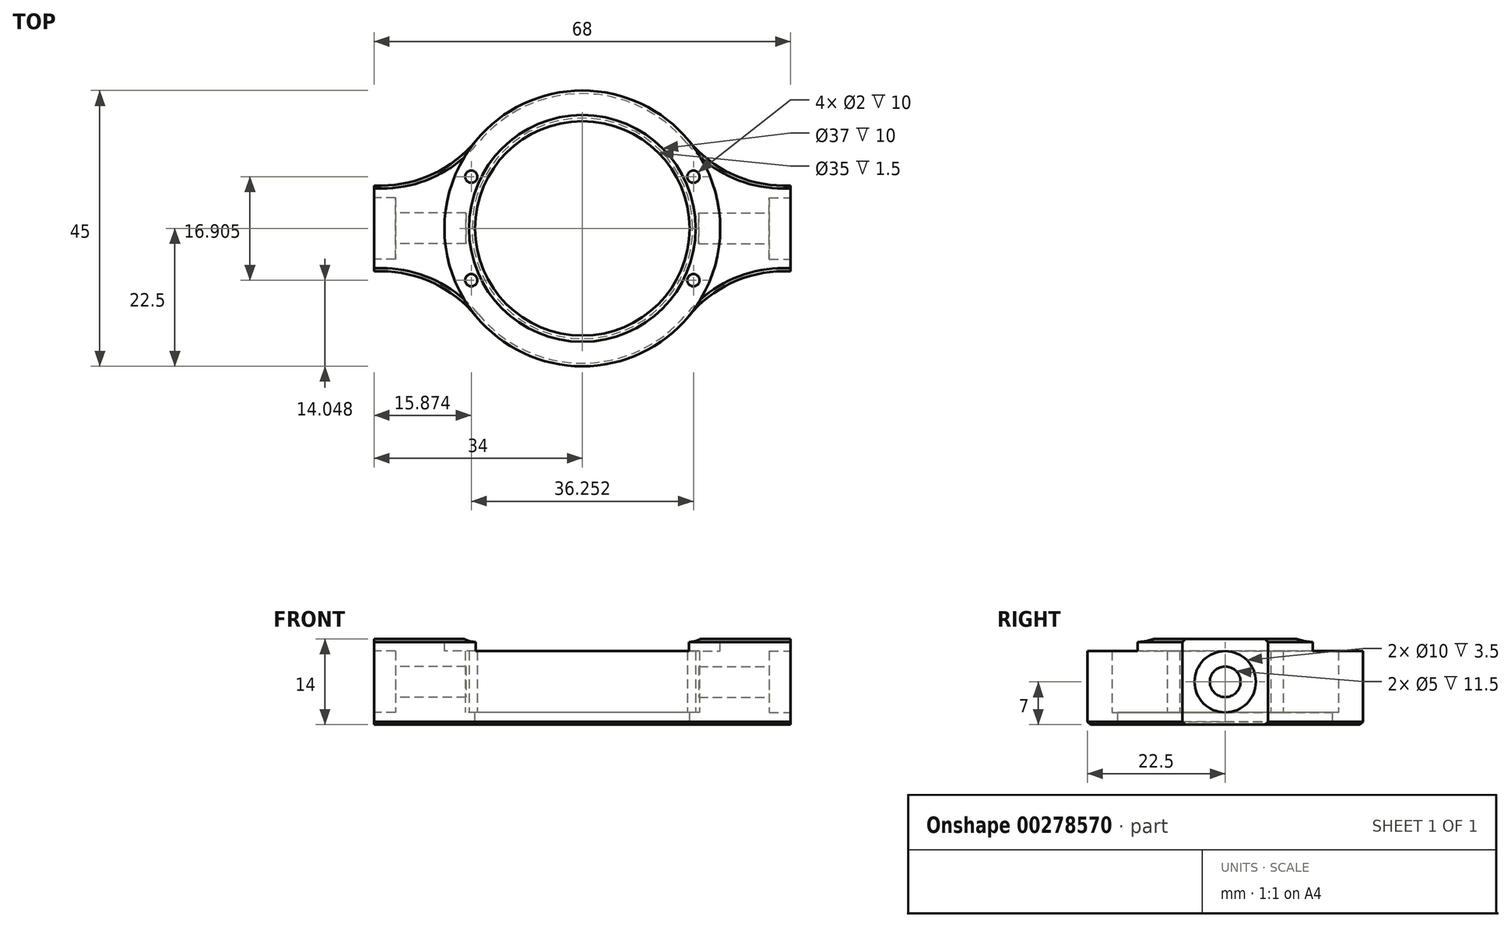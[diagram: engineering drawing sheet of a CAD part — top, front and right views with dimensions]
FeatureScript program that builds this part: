
annotation { "Feature Type Name" : "Feature", "Feature Type Description" : "" }
export const myFeature = defineFeature(function(context is Context, id is Id, definition is map)
    precondition{}
    {
        {
            var Q0;
            Q0=qCreatedBy(makeId("Top.planeOp"),FACE);
            var sketch = newSketch(context, id + "F0", { "sketchPlane" : qUnion([Q0])});
            skCircle(sketch, "E0", {"center": v(0, 0) * mm, "radius": 18.5 * mm});
            skArc(sketch, "E1", {"start": v(21.38, 7) * mm, "mid": v(0, 22.5) * mm, "end": v(-21.38, 7) * mm});
            skLineSegment(sketch, "E2.bottom", {"start": v(34, -7) * mm, "end": v(21.38, -7) * mm});
            skLineSegment(sketch, "E2.top", {"start": v(34, 7) * mm, "end": v(21.38, 7) * mm});
            skLineSegment(sketch, "E2.left", {"start": v(34, -7) * mm, "end": v(34, 7) * mm});
            skLineSegment(sketch, "E2.right", {"start": v(-34, -7) * mm, "end": v(-34, 7) * mm});
            skLineSegment(sketch, "E3.trimOffspring", {"start": v(-21.38, 7) * mm, "end": v(-34, 7) * mm});
            skLineSegment(sketch, "E4.trimOffspring", {"start": v(-21.38, -7) * mm, "end": v(-34, -7) * mm});
            skArc(sketch, "E5.trimOffspring", {"start": v(-21.38, -7) * mm, "mid": v(0, -22.5) * mm, "end": v(21.38, -7) * mm});
            skCircle(sketch, "E6", {"center": v(0, 0) * mm, "radius": 17.5 * mm});
            skLineSegment(sketch, "E7", {"start": v(-80.46, 0) * mm, "end": v(70.78, 0) * mm, "construction": true});
            skLineSegment(sketch, "E8", {"start": v(-80.46, -37.52) * mm, "end": v(70.78, 33) * mm, "construction": true});
            skLineSegment(sketch, "E9", {"start": v(-80.46, 37.52) * mm, "end": v(70.78, -33) * mm, "construction": true});
            skCircle(sketch, "E10", {"center": v(0, 0) * mm, "radius": 20 * mm, "construction": true});
            skCircle(sketch, "E11", {"center": v(18.13, 8.45) * mm, "radius": 1 * mm});
            skCircle(sketch, "E12", {"center": v(18.13, -8.45) * mm, "radius": 1 * mm});
            skCircle(sketch, "E13", {"center": v(-18.13, -8.45) * mm, "radius": 1 * mm});
            skCircle(sketch, "E14", {"center": v(-18.13, 8.45) * mm, "radius": 1 * mm});
            skSolve(sketch);
        }
        {
            var Q0;
            Q0 = qSketchRegion(id + "F0", true);
            extrude(context, id + "F1", {"entities" : qUnion([Q0]), "depth" : 7 * mm, "hasSecondDirection" : true, "secondDirectionOppositeDirection" : true, "secondDirectionDepth" : 7 * mm});
        }
        {
            var Q0;
            Q0=makeQuery(id+"F0.imprint","IMPRINT",FACE,{"disambiguationData":[TD([[makeQuery(id+"F0.imprint","IMPRINT",EDGE,{"derivedFrom":sQuery(id+"F0.wireOp",EDGE,"E0")}),1.0]])]});
            var Q1;
            Q1=makeQuery(id+"F0.imprint","IMPRINT",FACE,{"disambiguationData":[TD([[makeQuery(id+"F0.imprint","IMPRINT",EDGE,{"derivedFrom":sQuery(id+"F0.wireOp",EDGE,"E11")}),1.0]])]});
            var Q2;
            Q2=makeQuery(id+"F0.imprint","IMPRINT",FACE,{"disambiguationData":[TD([[makeQuery(id+"F0.imprint","IMPRINT",EDGE,{"derivedFrom":sQuery(id+"F0.wireOp",EDGE,"E12")}),1.0]])]});
            var Q3;
            Q3=makeQuery(id+"F0.imprint","IMPRINT",FACE,{"disambiguationData":[TD([[makeQuery(id+"F0.imprint","IMPRINT",EDGE,{"derivedFrom":sQuery(id+"F0.wireOp",EDGE,"E13")}),1.0]])]});
            var Q4;
            Q4=makeQuery(id+"F0.imprint","IMPRINT",FACE,{"disambiguationData":[TD([[makeQuery(id+"F0.imprint","IMPRINT",EDGE,{"derivedFrom":sQuery(id+"F0.wireOp",EDGE,"E14")}),1.0]])]});
            extrude(context, id + "F2", {"entities" : qUnion([Q0, Q1, Q2, Q3, Q4]), "operationType" : NewBodyOperationType.ADD, "oppositeDirection" : true, "depth" : 7 * mm, "hasSecondDirection" : true, "secondDirectionOppositeDirection" : false, "secondDirectionDepth" : -5 * mm});
        }
        {
            var Q0;
            Q0=makeQuery(id+"F1.opExtrude","SWEPT_EDGE",EDGE,{"disambiguationData":[OSD([sQuery(id+"F0.wireOp",EDGE,"E1"),sQuery(id+"F0.wireOp",EDGE,"E2.top")])]});
            var Q1;
            Q1=makeQuery(id+"F1.opExtrude","SWEPT_EDGE",EDGE,{"disambiguationData":[OSD([sQuery(id+"F0.wireOp",EDGE,"E2.bottom"),sQuery(id+"F0.wireOp",EDGE,"E5.trimOffspring")])]});
            var Q2;
            Q2=makeQuery(id+"F1.opExtrude","SWEPT_EDGE",EDGE,{"disambiguationData":[OSD([sQuery(id+"F0.wireOp",EDGE,"E4.trimOffspring"),sQuery(id+"F0.wireOp",EDGE,"E5.trimOffspring")])]});
            var Q3;
            Q3=makeQuery(id+"F1.opExtrude","SWEPT_EDGE",EDGE,{"disambiguationData":[OSD([sQuery(id+"F0.wireOp",EDGE,"E1"),sQuery(id+"F0.wireOp",EDGE,"E3.trimOffspring")])]});
            fillet(context, id + "F3", {"entities" : qUnion([Q0, Q1, Q2, Q3]), "radius" : 20 * mm, "tangentPropagation" : true, "allowEdgeOverflow" : false});
        }
        {
            var Q0;
            Q0=makeQuery(id+"F1.opExtrude","CAP_FACE",FACE,{"disambiguationData":[OSD([sQuery(id+"F0.wireOp",EDGE,"E0"),sQuery(id+"F0.wireOp",EDGE,"E1"),sQuery(id+"F0.wireOp",EDGE,"E2.bottom"),sQuery(id+"F0.wireOp",EDGE,"E2.top"),sQuery(id+"F0.wireOp",EDGE,"E2.left"),sQuery(id+"F0.wireOp",EDGE,"E2.right"),sQuery(id+"F0.wireOp",EDGE,"E3.trimOffspring"),sQuery(id+"F0.wireOp",EDGE,"E4.trimOffspring"),sQuery(id+"F0.wireOp",EDGE,"E5.trimOffspring")])],"isStart":false});
            var sketch = newSketch(context, id + "F4", { "sketchPlane" : qUnion([Q0])});
            skCircle(sketch, "E15", {"center": v(0, 0) * mm, "radius": 22.5 * mm});
            skCircle(sketch, "E16", {"center": v(0, 0) * mm, "radius": 17.5 * mm});
            skLineSegment(sketch, "E17", {"start": v(43.77, 0) * mm, "end": v(-49.2, 0) * mm, "construction": true});
            skPoint(sketch, "E17.startSnap0", {"position": v(-34, 0) * mm});
            skPoint(sketch, "E17.endSnap0", {"position": v(-34, 0) * mm});
            skLineSegment(sketch, "E18", {"start": v(-49.2, -22.95) * mm, "end": v(43.77, 20.41) * mm, "construction": true});
            skLineSegment(sketch, "E19", {"start": v(-49.2, 22.95) * mm, "end": v(43.77, -20.41) * mm, "construction": true});
            skCircle(sketch, "E20", {"center": v(0, 0) * mm, "radius": 20 * mm, "construction": true});
            skCircle(sketch, "E21", {"center": v(18.13, 8.45) * mm, "radius": 1 * mm});
            skCircle(sketch, "E22", {"center": v(18.13, -8.45) * mm, "radius": 1 * mm});
            skCircle(sketch, "E23", {"center": v(-18.13, 8.45) * mm, "radius": 1 * mm});
            skCircle(sketch, "E24", {"center": v(-18.13, -8.45) * mm, "radius": 1 * mm});
            skSolve(sketch);
        }
        {
            var Q0;
            {var subQ7=sQuery(id+"F0.wireOp",EDGE,"E0");Q0=makeQuery(id+"F4.imprint","IMPRINT",FACE,{"disambiguationData":[TD([[makeQuery(id+"F4.imprint","IMPRINT",EDGE,{"derivedFrom":makeQuery(id+"F1.opExtrude","CAP_EDGE",EDGE,{"disambiguationData":[OSD([subQ7])],"isStart":false})}),-1.0]])]});}
            var Q1;
            Q1=makeQuery(id+"F4.imprint","IMPRINT",FACE,{"disambiguationData":[TD([[makeQuery(id+"F4.imprint","IMPRINT",EDGE,{"derivedFrom":sQuery(id+"F4.wireOp",EDGE,"E22")}),1.0]])]});
            var Q2;
            Q2=makeQuery(id+"F4.imprint","IMPRINT",FACE,{"disambiguationData":[TD([[makeQuery(id+"F4.imprint","IMPRINT",EDGE,{"derivedFrom":sQuery(id+"F4.wireOp",EDGE,"E21")}),1.0]])]});
            var Q3;
            Q3=makeQuery(id+"F4.imprint","IMPRINT",FACE,{"disambiguationData":[TD([[makeQuery(id+"F4.imprint","IMPRINT",EDGE,{"derivedFrom":sQuery(id+"F4.wireOp",EDGE,"E23")}),1.0]])]});
            var Q4;
            Q4=makeQuery(id+"F4.imprint","IMPRINT",FACE,{"disambiguationData":[TD([[makeQuery(id+"F4.imprint","IMPRINT",EDGE,{"derivedFrom":sQuery(id+"F4.wireOp",EDGE,"E24")}),1.0]])]});
            extrude(context, id + "F5", {"entities" : qUnion([Q0, Q1, Q2, Q3, Q4]), "operationType" : NewBodyOperationType.REMOVE, "oppositeDirection" : true, "depth" : 2 * mm});
        }
        {
            var Q0;
            {var subQ7=sQuery(id+"F0.wireOp",EDGE,"E0");Q0=makeQuery(id+"F4.imprint","IMPRINT",FACE,{"disambiguationData":[TD([[makeQuery(id+"F4.imprint","IMPRINT",EDGE,{"derivedFrom":makeQuery(id+"F1.opExtrude","CAP_EDGE",EDGE,{"disambiguationData":[OSD([subQ7])],"isStart":false})}),-1.0]])]});}
            var Q1;
            Q1=makeQuery(id+"F4.imprint","IMPRINT",FACE,{"disambiguationData":[TD([[makeQuery(id+"F4.imprint","IMPRINT",EDGE,{"derivedFrom":sQuery(id+"F4.wireOp",EDGE,"E16")}),-1.0]])]});
            extrude(context, id + "F6", {"entities" : qUnion([Q0, Q1]), "depth" : -2 * mm});
        }
        {
            var Q0;
            {var subQ0=sQuery(id+"F0.wireOp",EDGE,"E5.trimOffspring");var subQ1=sQuery(id+"F0.wireOp",EDGE,"E4.trimOffspring");Q0=makeQuery(id+"F3.opFillet","BLEND_EDGE",EDGE,{"blendedFrom":[makeQuery(id+"F1.opExtrude","SWEPT_EDGE",EDGE,{"disambiguationData":[OSD([subQ1,subQ0])]}),makeQuery(id+"F1.opExtrude","CAP_FACE",FACE,{"disambiguationData":[OSD([sQuery(id+"F0.wireOp",EDGE,"E0"),sQuery(id+"F0.wireOp",EDGE,"E1"),sQuery(id+"F0.wireOp",EDGE,"E2.bottom"),sQuery(id+"F0.wireOp",EDGE,"E2.top"),sQuery(id+"F0.wireOp",EDGE,"E2.left"),sQuery(id+"F0.wireOp",EDGE,"E2.right"),sQuery(id+"F0.wireOp",EDGE,"E3.trimOffspring"),subQ1,subQ0])],"isStart":false})],"blendedInto":[makeQuery(id+"F1.opExtrude","CAP_FACE",FACE,{"disambiguationData":[OSD([sQuery(id+"F0.wireOp",EDGE,"E0"),sQuery(id+"F0.wireOp",EDGE,"E1"),sQuery(id+"F0.wireOp",EDGE,"E2.bottom"),sQuery(id+"F0.wireOp",EDGE,"E2.top"),sQuery(id+"F0.wireOp",EDGE,"E2.left"),sQuery(id+"F0.wireOp",EDGE,"E2.right"),sQuery(id+"F0.wireOp",EDGE,"E3.trimOffspring"),subQ1,subQ0])],"isStart":false})]});}
            var Q1;
            {var subQ0=sQuery(id+"F0.wireOp",EDGE,"E3.trimOffspring");var subQ1=sQuery(id+"F0.wireOp",EDGE,"E1");Q1=makeQuery(id+"F3.opFillet","BLEND_EDGE",EDGE,{"blendedFrom":[makeQuery(id+"F1.opExtrude","SWEPT_EDGE",EDGE,{"disambiguationData":[OSD([subQ1,subQ0])]}),makeQuery(id+"F1.opExtrude","CAP_FACE",FACE,{"disambiguationData":[OSD([sQuery(id+"F0.wireOp",EDGE,"E0"),subQ1,sQuery(id+"F0.wireOp",EDGE,"E2.bottom"),sQuery(id+"F0.wireOp",EDGE,"E2.top"),sQuery(id+"F0.wireOp",EDGE,"E2.left"),sQuery(id+"F0.wireOp",EDGE,"E2.right"),subQ0,sQuery(id+"F0.wireOp",EDGE,"E4.trimOffspring"),sQuery(id+"F0.wireOp",EDGE,"E5.trimOffspring")])],"isStart":false})],"blendedInto":[makeQuery(id+"F1.opExtrude","CAP_FACE",FACE,{"disambiguationData":[OSD([sQuery(id+"F0.wireOp",EDGE,"E0"),subQ1,sQuery(id+"F0.wireOp",EDGE,"E2.bottom"),sQuery(id+"F0.wireOp",EDGE,"E2.top"),sQuery(id+"F0.wireOp",EDGE,"E2.left"),sQuery(id+"F0.wireOp",EDGE,"E2.right"),subQ0,sQuery(id+"F0.wireOp",EDGE,"E4.trimOffspring"),sQuery(id+"F0.wireOp",EDGE,"E5.trimOffspring")])],"isStart":false})]});}
            var Q2;
            {var subQ0=sQuery(id+"F0.wireOp",EDGE,"E5.trimOffspring");var subQ1=sQuery(id+"F0.wireOp",EDGE,"E2.bottom");Q2=makeQuery(id+"F3.opFillet","BLEND_EDGE",EDGE,{"blendedFrom":[makeQuery(id+"F1.opExtrude","SWEPT_EDGE",EDGE,{"disambiguationData":[OSD([subQ1,subQ0])]}),makeQuery(id+"F1.opExtrude","CAP_FACE",FACE,{"disambiguationData":[OSD([sQuery(id+"F0.wireOp",EDGE,"E0"),sQuery(id+"F0.wireOp",EDGE,"E1"),subQ1,sQuery(id+"F0.wireOp",EDGE,"E2.top"),sQuery(id+"F0.wireOp",EDGE,"E2.left"),sQuery(id+"F0.wireOp",EDGE,"E2.right"),sQuery(id+"F0.wireOp",EDGE,"E3.trimOffspring"),sQuery(id+"F0.wireOp",EDGE,"E4.trimOffspring"),subQ0])],"isStart":false})],"blendedInto":[makeQuery(id+"F1.opExtrude","CAP_FACE",FACE,{"disambiguationData":[OSD([sQuery(id+"F0.wireOp",EDGE,"E0"),sQuery(id+"F0.wireOp",EDGE,"E1"),subQ1,sQuery(id+"F0.wireOp",EDGE,"E2.top"),sQuery(id+"F0.wireOp",EDGE,"E2.left"),sQuery(id+"F0.wireOp",EDGE,"E2.right"),sQuery(id+"F0.wireOp",EDGE,"E3.trimOffspring"),sQuery(id+"F0.wireOp",EDGE,"E4.trimOffspring"),subQ0])],"isStart":false})]});}
            var Q3;
            {var subQ0=sQuery(id+"F0.wireOp",EDGE,"E2.top");var subQ1=sQuery(id+"F0.wireOp",EDGE,"E1");Q3=makeQuery(id+"F3.opFillet","BLEND_EDGE",EDGE,{"blendedFrom":[makeQuery(id+"F1.opExtrude","SWEPT_EDGE",EDGE,{"disambiguationData":[OSD([subQ1,subQ0])]}),makeQuery(id+"F1.opExtrude","CAP_FACE",FACE,{"disambiguationData":[OSD([sQuery(id+"F0.wireOp",EDGE,"E0"),subQ1,sQuery(id+"F0.wireOp",EDGE,"E2.bottom"),subQ0,sQuery(id+"F0.wireOp",EDGE,"E2.left"),sQuery(id+"F0.wireOp",EDGE,"E2.right"),sQuery(id+"F0.wireOp",EDGE,"E3.trimOffspring"),sQuery(id+"F0.wireOp",EDGE,"E4.trimOffspring"),sQuery(id+"F0.wireOp",EDGE,"E5.trimOffspring")])],"isStart":false})],"blendedInto":[makeQuery(id+"F1.opExtrude","CAP_FACE",FACE,{"disambiguationData":[OSD([sQuery(id+"F0.wireOp",EDGE,"E0"),subQ1,sQuery(id+"F0.wireOp",EDGE,"E2.bottom"),subQ0,sQuery(id+"F0.wireOp",EDGE,"E2.left"),sQuery(id+"F0.wireOp",EDGE,"E2.right"),sQuery(id+"F0.wireOp",EDGE,"E3.trimOffspring"),sQuery(id+"F0.wireOp",EDGE,"E4.trimOffspring"),sQuery(id+"F0.wireOp",EDGE,"E5.trimOffspring")])],"isStart":false})]});}
            var Q4;
            {var subQ0=sQuery(id+"F0.wireOp",EDGE,"E0");var subQ1=sQuery(id+"F0.wireOp",EDGE,"E5.trimOffspring");var subQ2=sQuery(id+"F0.wireOp",EDGE,"E2.bottom");Q4=makeQuery(id+"F3.opFillet","BLEND_EDGE",EDGE,{"blendedFrom":[makeQuery(id+"F1.opExtrude","SWEPT_EDGE",EDGE,{"disambiguationData":[OSD([subQ2,subQ1])]}),makeQuery(id+"F2.boolean.opBoolean","MERGE",FACE,{"derivedFrom":[makeQuery(id+"F1.opExtrude","CAP_FACE",FACE,{"disambiguationData":[OSD([subQ0,sQuery(id+"F0.wireOp",EDGE,"E1"),subQ2,sQuery(id+"F0.wireOp",EDGE,"E2.top"),sQuery(id+"F0.wireOp",EDGE,"E2.left"),sQuery(id+"F0.wireOp",EDGE,"E2.right"),sQuery(id+"F0.wireOp",EDGE,"E3.trimOffspring"),sQuery(id+"F0.wireOp",EDGE,"E4.trimOffspring"),subQ1])],"isStart":true}),makeQuery(id+"F2.opExtrude","CAP_FACE",FACE,{"disambiguationData":[OSD([subQ0,sQuery(id+"F0.wireOp",EDGE,"E6")])],"isStart":false})]})],"blendedInto":[makeQuery(id+"F2.boolean.opBoolean","MERGE",FACE,{"derivedFrom":[makeQuery(id+"F1.opExtrude","CAP_FACE",FACE,{"disambiguationData":[OSD([subQ0,sQuery(id+"F0.wireOp",EDGE,"E1"),subQ2,sQuery(id+"F0.wireOp",EDGE,"E2.top"),sQuery(id+"F0.wireOp",EDGE,"E2.left"),sQuery(id+"F0.wireOp",EDGE,"E2.right"),sQuery(id+"F0.wireOp",EDGE,"E3.trimOffspring"),sQuery(id+"F0.wireOp",EDGE,"E4.trimOffspring"),subQ1])],"isStart":true}),makeQuery(id+"F2.opExtrude","CAP_FACE",FACE,{"disambiguationData":[OSD([subQ0,sQuery(id+"F0.wireOp",EDGE,"E6")])],"isStart":false})]})]});}
            var Q5;
            Q5=makeQuery(id+"F1.opExtrude","CAP_EDGE",EDGE,{"disambiguationData":[OSD([sQuery(id+"F0.wireOp",EDGE,"E1")])],"isStart":true});
            var Q6;
            Q6=makeQuery(id+"F2.opExtrude","CAP_EDGE",EDGE,{"disambiguationData":[OSD([sQuery(id+"F0.wireOp",EDGE,"E6")])],"isStart":false});
            var Q7;
            Q7=makeQuery(id+"F5.boolean.opBoolean","COPY",EDGE,{"derivedFrom":makeQuery(id+"F5.opExtrude","CAP_EDGE",EDGE,{"disambiguationData":[OSD([sQuery(id+"F0.wireOp",EDGE,"E0")])],"isStart":false})});
            chamfer(context, id + "F7", {"entities" : qUnion([Q0, Q1, Q2, Q3, Q4, Q5, Q6, Q7]), "width" : 0.5 * mm, "tangentPropagation" : true});
        }
        {
            var Q0;
            Q0=makeQuery(id+"F6.opExtrude","CAP_EDGE",EDGE,{"disambiguationData":[OSD([sQuery(id+"F4.wireOp",EDGE,"E21")])],"isStart":true});
            var Q1;
            Q1=makeQuery(id+"F6.opExtrude","CAP_EDGE",EDGE,{"disambiguationData":[OSD([sQuery(id+"F4.wireOp",EDGE,"E22")])],"isStart":true});
            var Q2;
            Q2=makeQuery(id+"F6.opExtrude","CAP_EDGE",EDGE,{"disambiguationData":[OSD([sQuery(id+"F4.wireOp",EDGE,"E24")])],"isStart":true});
            var Q3;
            Q3=makeQuery(id+"F6.opExtrude","CAP_EDGE",EDGE,{"disambiguationData":[OSD([sQuery(id+"F4.wireOp",EDGE,"E23")])],"isStart":true});
            chamfer(context, id + "F8", {"entities" : qUnion([Q0, Q1, Q2, Q3]), "width" : 1 * mm, "tangentPropagation" : true});
        }
        {
            var Q0;
            Q0=makeQuery(id+"F1.opExtrude","SWEPT_FACE",FACE,{"disambiguationData":[OSD([sQuery(id+"F0.wireOp",EDGE,"E2.right")])]});
            var sketch = newSketch(context, id + "F9", { "sketchPlane" : qUnion([Q0])});
            skCircle(sketch, "E25", {"center": v(0, 0) * mm, "radius": 5 * mm});
            skCircle(sketch, "E26", {"center": v(0, 0) * mm, "radius": 2.5 * mm});
            skSolve(sketch);
        }
        {
            var Q0;
            Q0=makeQuery(id+"F9.imprint","IMPRINT",FACE,{"disambiguationData":[TD([[makeQuery(id+"F9.imprint","IMPRINT",EDGE,{"derivedFrom":sQuery(id+"F9.wireOp",EDGE,"E25")}),1.0]])]});
            var Q1;
            Q1=makeQuery(id+"F9.imprint","IMPRINT",FACE,{"disambiguationData":[TD([[makeQuery(id+"F9.imprint","IMPRINT",EDGE,{"derivedFrom":sQuery(id+"F9.wireOp",EDGE,"E26")}),1.0]])]});
            extrude(context, id + "F10", {"entities" : qUnion([Q0, Q1]), "operationType" : NewBodyOperationType.REMOVE, "oppositeDirection" : true, "depth" : 3.5 * mm});
        }
        {
            var Q0;
            Q0=makeQuery(id+"F9.imprint","IMPRINT",FACE,{"disambiguationData":[TD([[makeQuery(id+"F9.imprint","IMPRINT",EDGE,{"derivedFrom":sQuery(id+"F9.wireOp",EDGE,"E26")}),1.0]])]});
            extrude(context, id + "F11", {"entities" : qUnion([Q0]), "operationType" : NewBodyOperationType.REMOVE, "oppositeDirection" : true, "depth" : 15 * mm});
        }
        {
            var Q0;
            Q0=makeQuery(id+"F1.opExtrude","SWEPT_BODY",BODY,{"disambiguationData":[OSD([sQuery(id+"F0.wireOp",EDGE,"E0"),sQuery(id+"F0.wireOp",EDGE,"E1"),sQuery(id+"F0.wireOp",EDGE,"E2.bottom"),sQuery(id+"F0.wireOp",EDGE,"E2.top"),sQuery(id+"F0.wireOp",EDGE,"E2.left"),sQuery(id+"F0.wireOp",EDGE,"E2.right"),sQuery(id+"F0.wireOp",EDGE,"E3.trimOffspring"),sQuery(id+"F0.wireOp",EDGE,"E4.trimOffspring"),sQuery(id+"F0.wireOp",EDGE,"E5.trimOffspring"),sQuery(id+"F0.wireOp",EDGE,"E11"),sQuery(id+"F0.wireOp",EDGE,"E12"),sQuery(id+"F0.wireOp",EDGE,"E13"),sQuery(id+"F0.wireOp",EDGE,"E14")])]});
            var Q1;
            Q1=qCreatedBy(makeId("Right.planeOp"),FACE);
            mirror(context, id + "F12", {"operationType" : NewBodyOperationType.INTERSECT, "entities" : qUnion([Q0]), "mirrorPlane" : qUnion([Q1])});
        }
    });
